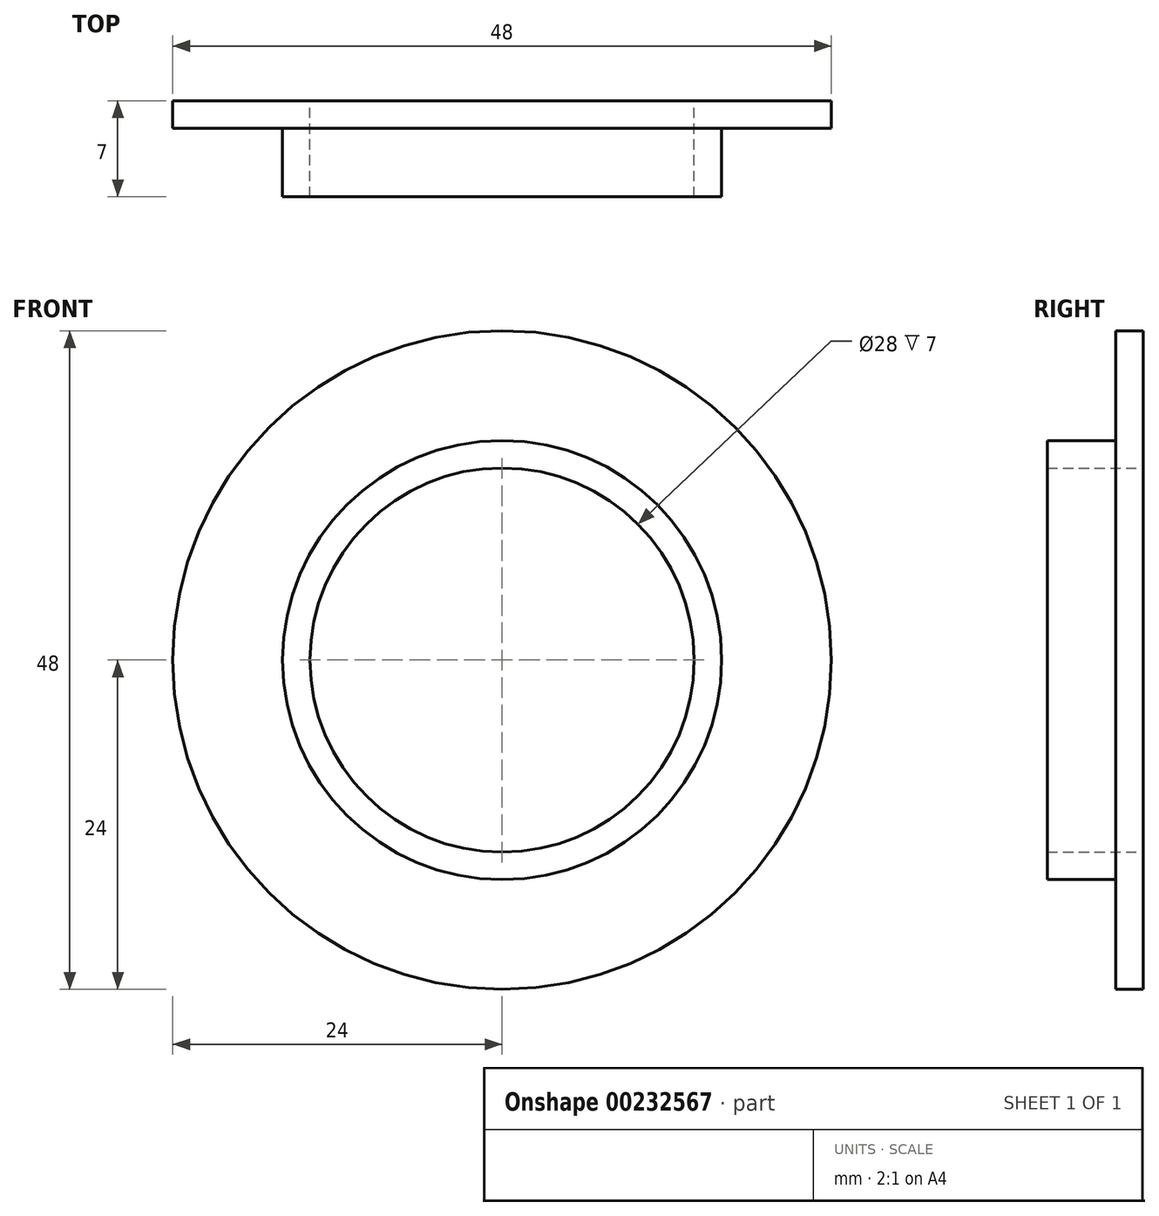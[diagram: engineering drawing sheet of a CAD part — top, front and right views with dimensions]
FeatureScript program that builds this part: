
annotation { "Feature Type Name" : "Feature", "Feature Type Description" : "" }
export const myFeature = defineFeature(function(context is Context, id is Id, definition is map)
    precondition{}
    {
        {
            var Q0;
            Q0=qCreatedBy(makeId("Front.planeOp"),FACE);
            var sketch = newSketch(context, id + "F0", { "sketchPlane" : qUnion([Q0])});
            skCircle(sketch, "E0", {"center": v(0, 0) * mm, "radius": 1 * mm});
            skCircle(sketch, "E1", {"center": v(0, 0) * mm, "radius": 14 * mm});
            skCircle(sketch, "E2", {"center": v(0, 0) * mm, "radius": 16 * mm});
            skCircle(sketch, "E3", {"center": v(0, 0) * mm, "radius": 24 * mm});
            skSolve(sketch);
        }
        {
            var Q0;
            Q0=makeQuery(id+"F0.imprint","IMPRINT",FACE,{"disambiguationData":[TD([[makeQuery(id+"F0.imprint","IMPRINT",EDGE,{"derivedFrom":sQuery(id+"F0.wireOp",EDGE,"E2")}),-1.0]])]});
            extrude(context, id + "F1", {"entities" : qUnion([Q0]), "depth" : 2 * mm});
        }
        {
            var Q0;
            Q0=makeQuery(id+"F0.imprint","IMPRINT",FACE,{"disambiguationData":[TD([[makeQuery(id+"F0.imprint","IMPRINT",EDGE,{"derivedFrom":sQuery(id+"F0.wireOp",EDGE,"E1")}),-1.0]])]});
            extrude(context, id + "F2", {"entities" : qUnion([Q0]), "operationType" : NewBodyOperationType.ADD, "depth" : 7 * mm});
        }
    });
